# Revit family: HVAC_Natural-Ventilation_Envira-North_Hurricane-Turbine_Roof-Turbine-Ventilation
name_source: partatom
category: Mechanical Equipment
units: mm (PartAtom-declared; Revit-internal decimal feet)

## family parameters
Always vertical = No
Classification = None
Cut with Voids When Loaded = No
Maintain Annotation Orientation = No
OmniClass Number = 23.75.35.21
OmniClass Title = Extractors
Part Type = Normal
Room Calculation Point = No
Round Connector Dimension = Use Diameter
Shared = No
Work Plane-Based = Yes

## types (6) — shared parameters
Actual Ventilation Air Flow = 0 CFM
Date Updated = 23/12/24
Default Elevation = 0"
Manufacturer = Envira-North Systems
Product Material = Envira North Systems - Metal - Aluminium
Product Page URL = https://www.enviranorth.com
URL = https://www.enviranorth.com
Version = 1

## per-type parameters (varying)
| type | Description | Exhaust Air Connection Diameter | Minimum Air Flow | Model | VariPitch Flue Section | Weight | z_A | z_Bmax | z_Bmin | z_C | z_D | z_E | z_F | z_F2 | z_Maximum Angle | z_OD |
| H300 - Hurricane | Hurricane Turbine | 12" | 572 CFM | EN900X2001
EN900X2001 | No | 9.30 lbf | 12 1/2" | 10" | 8 3/4" | 6 1/4" | 11 51/64" | 6 1/2" | 19 5/8" | 23 5/8" | 0.00° | 18 1/2" |
| H700 - Hurricane | Hurricane Turbine | 27" | 1589 CFM | EN900X0701 | No | 34.80 lbf | 21 29/32" | 12" | 10" | 12 1/4" | 27 23/64" | 12 3/4" | 39 3/8" | 39 3/8" | 0.00° | 34 1/2" |
| H900 - Hurricane | Hurricane Turbine | 36" | 3305 CFM | EN900X0001 | No | 63.00 lbf | 25 1/4" | 19 3/8" | 19 3/8" | 12 1/4" | 27 23/64" | 12 3/4" | 47 1/4" | 47 1/4" | 0.00° | 43" |
| H300 - Hurricane Vari-Pitch | Hurricane Turbine Vari-Pitch | 12" | 572 CFM | EN900X2002
EN900X2001 | Yes | 9.30 lbf | 12 1/2" | 10" | 8 3/4" | 7 1/2" | 12" | 6 1/2" | 19 5/8" | 23 5/8" | 45.00° | 18 1/2" |
| H700 - Hurricane Vari-Pitch | Hurricane Turbine Vari-Pitch | 27" | 1589 CFM | EN900X0702 | Yes | 34.80 lbf | 21 29/32" | 12" | 10" | 13 51/64" | 27 23/64" | 12 3/4" | 39 3/8" | 39 3/8" | 45.00° | 34 1/2" |
| H900 - Hurricane Vari-Pitch | Hurricane Turbine Vari-Pitch | 36" | 3305 CFM | EN900X0002 | Yes | 63.00 lbf | 25 1/4" | 19 3/8" | 19 3/8" | 15 13/32" | 35 1/4" | 12 3/4" | 47 1/4" | 47 1/4" | 22.50° | 43" |

## geometry (parser evidence)
native form markers: Sweep x5
no freeform markers — native parametric forms only
